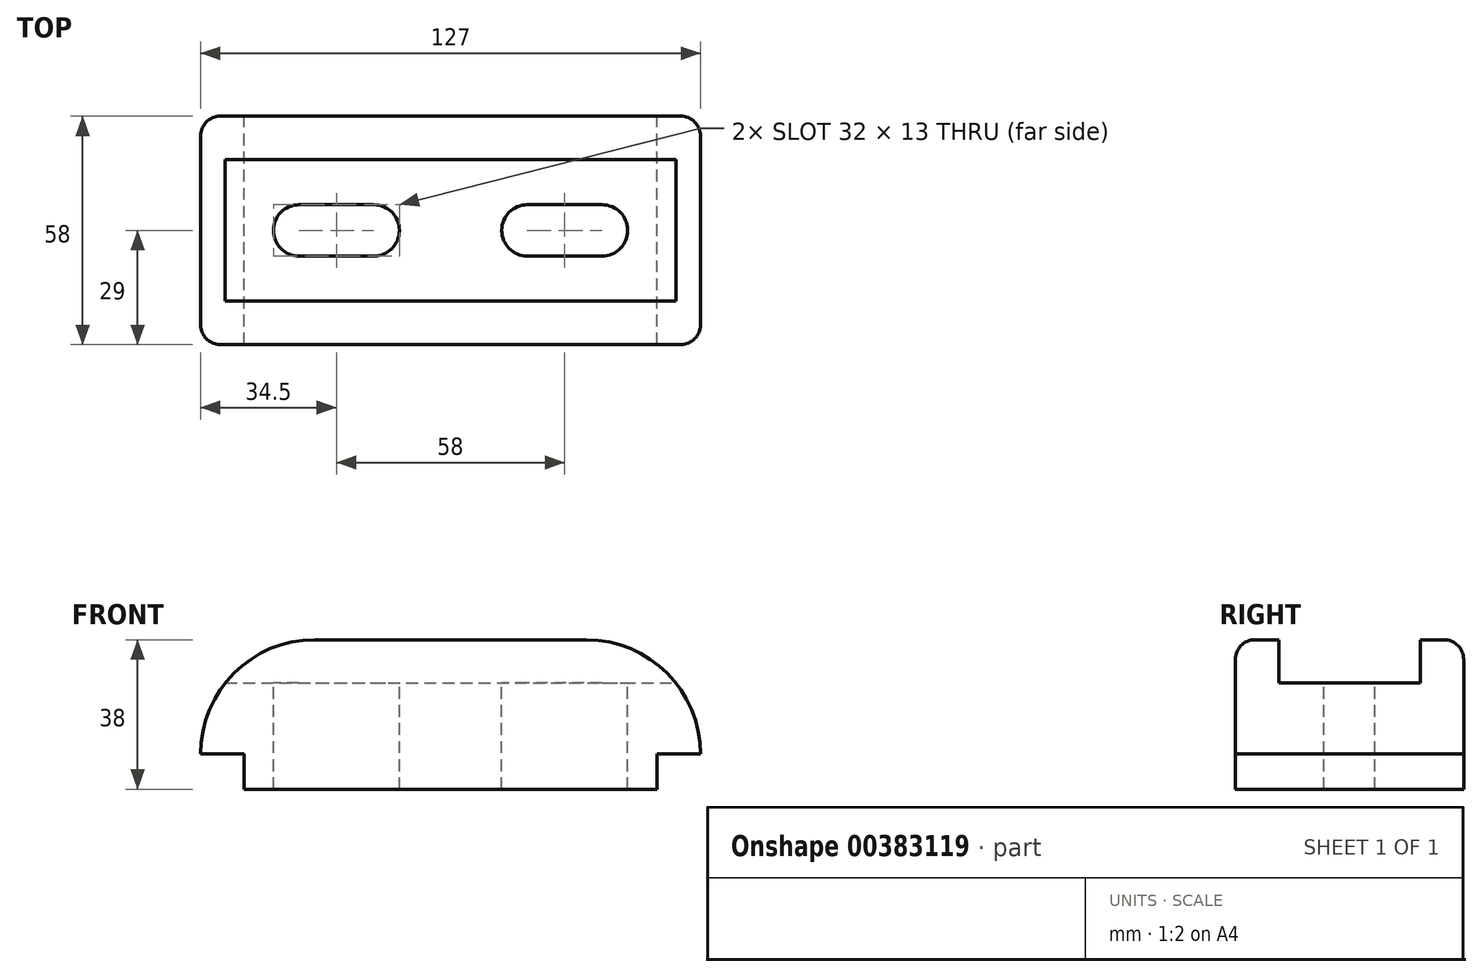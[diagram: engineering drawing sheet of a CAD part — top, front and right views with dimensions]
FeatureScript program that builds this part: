
annotation { "Feature Type Name" : "Feature", "Feature Type Description" : "" }
export const myFeature = defineFeature(function(context is Context, id is Id, definition is map)
    precondition{}
    {
        {
            var Q0;
            Q0=qCreatedBy(makeId("Front.planeOp"),FACE);
            var sketch = newSketch(context, id + "F0", { "sketchPlane" : qUnion([Q0])});
            skLineSegment(sketch, "E0", {"start": v(0, 0) * mm, "end": v(52.5, 0) * mm});
            skLineSegment(sketch, "E1", {"start": v(0, 0) * mm, "end": v(-52.5, 0) * mm});
            skLineSegment(sketch, "E2", {"start": v(-52.5, 0) * mm, "end": v(-52.5, 9) * mm});
            skLineSegment(sketch, "E3", {"start": v(52.5, 0) * mm, "end": v(52.5, 9) * mm});
            skLineSegment(sketch, "E4", {"start": v(52.5, 9) * mm, "end": v(63.5, 9) * mm});
            skLineSegment(sketch, "E5", {"start": v(-52.5, 9) * mm, "end": v(-63.5, 9) * mm});
            skLineSegment(sketch, "E6", {"start": v(0, 0) * mm, "end": v(0, 38) * mm});
            skArc(sketch, "E7", {"start": v(63.5, 9) * mm, "mid": v(55, 29.5) * mm, "end": v(34.5, 38) * mm});
            skArc(sketch, "E8", {"start": v(-34.5, 38) * mm, "mid": v(-55, 29.5) * mm, "end": v(-63.5, 9) * mm});
            skLineSegment(sketch, "E9", {"start": v(-34.5, 38) * mm, "end": v(34.5, 38) * mm});
            skSolve(sketch);
        }
        {
            var Q0;
            Q0 = qSketchRegion(id + "F0", true);
            extrude(context, id + "F1", {"entities" : qUnion([Q0]), "depth" : 58 * mm});
        }
        {
            var Q0;
            Q0=qCreatedBy(makeId("Right.planeOp"),FACE);
            var sketch = newSketch(context, id + "F2", { "sketchPlane" : qUnion([Q0])});
            skLineSegment(sketch, "E10.bottom", {"start": v(-47, 38) * mm, "end": v(-11, 38) * mm});
            skLineSegment(sketch, "E10.top", {"start": v(-47, 27) * mm, "end": v(-11, 27) * mm});
            skLineSegment(sketch, "E10.left", {"start": v(-47, 38) * mm, "end": v(-47, 27) * mm});
            skLineSegment(sketch, "E10.right", {"start": v(-11, 38) * mm, "end": v(-11, 27) * mm});
            skSolve(sketch);
        }
        {
            var Q0;
            Q0 = qSketchRegion(id + "F2", true);
            extrude(context, id + "F3", {"entities" : qUnion([Q0]), "operationType" : NewBodyOperationType.REMOVE, "endBound" : BoundingType.THROUGH_ALL, "oppositeDirection" : true, "depth" : 1000 * mm, "hasSecondDirection" : true, "secondDirectionBound" : SecondDirectionBoundingType.THROUGH_ALL, "secondDirectionOppositeDirection" : false, "secondDirectionDepth" : 25 * mm});
        }
        {
            var Q0;
            Q0=makeQuery(id+"F3.boolean.opBoolean","COPY",FACE,{"derivedFrom":makeQuery(id+"F3.opExtrude","SWEPT_FACE",FACE,{"disambiguationData":[OSD([sQuery(id+"F2.wireOp",EDGE,"E10.top")])]})});
            var sketch = newSketch(context, id + "F4", { "sketchPlane" : qUnion([Q0])});
            skLineSegment(sketch, "E11", {"start": v(57.24, -47) * mm, "end": v(57.24, -11) * mm, "construction": true});
            skLineSegment(sketch, "E12", {"start": v(-57.24, -47) * mm, "end": v(-57.24, -29) * mm, "construction": true});
            skArc(sketch, "E13", {"start": v(-38.5, -22.5) * mm, "mid": v(-45, -29) * mm, "end": v(-38.5, -35.5) * mm});
            skArc(sketch, "E14", {"start": v(-19.5, -35.5) * mm, "mid": v(-13, -29) * mm, "end": v(-19.5, -22.5) * mm});
            skArc(sketch, "E15", {"start": v(19.5, -22.5) * mm, "mid": v(13, -29) * mm, "end": v(19.5, -35.5) * mm});
            skArc(sketch, "E16", {"start": v(38.5, -35.5) * mm, "mid": v(45, -29) * mm, "end": v(38.5, -22.5) * mm});
            skLineSegment(sketch, "E17", {"start": v(-38.5, -22.5) * mm, "end": v(-19.5, -22.5) * mm});
            skLineSegment(sketch, "E18", {"start": v(-38.5, -35.5) * mm, "end": v(-19.5, -35.5) * mm});
            skLineSegment(sketch, "E19", {"start": v(38.5, -35.5) * mm, "end": v(19.5, -35.5) * mm});
            skLineSegment(sketch, "E20", {"start": v(38.5, -22.5) * mm, "end": v(19.5, -22.5) * mm});
            skSolve(sketch);
        }
        {
            var Q0;
            Q0 = qSketchRegion(id + "F4", true);
            extrude(context, id + "F5", {"entities" : qUnion([Q0]), "operationType" : NewBodyOperationType.REMOVE, "endBound" : BoundingType.THROUGH_ALL, "oppositeDirection" : true, "depth" : 25 * mm});
        }
        {
            var Q0;
            Q0=makeQuery(id+"F1.opExtrude","CAP_EDGE",EDGE,{"disambiguationData":[OSD([sQuery(id+"F0.wireOp",EDGE,"E9")])],"isStart":false});
            var Q1;
            Q1=makeQuery(id+"F1.opExtrude","CAP_EDGE",EDGE,{"disambiguationData":[OSD([sQuery(id+"F0.wireOp",EDGE,"E9")])],"isStart":true});
            fillet(context, id + "F6", {"entities" : qUnion([Q0, Q1]), "radius" : 5 * mm, "tangentPropagation" : true, "allowEdgeOverflow" : false});
        }
    });
